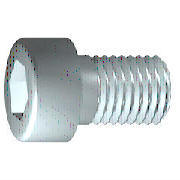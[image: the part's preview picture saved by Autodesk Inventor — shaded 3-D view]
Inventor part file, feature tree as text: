
AUTODESK INVENTOR PART (.ipt)
format: ipt  version: 2015 (Build 190159000, 159)  size: 190,464 bytes
history: native  units: mm (DEFAULTED — no unit token found)
features: sketch x2, other x1, extrude x1, plane x1, fillet x1
ambient origin geometry x7: Origin, YZ Plane, XY Plane, X Axis, Y Axis, Z Axis, Center Point
bodies: Body1 (feature_tree)
feature tree (6):
  other  "Bryła"
  extrude  "Szczelina"  Depth=27.5mm
  plane  "Work Plane1"
  fillet  "Fillet2"  Radius=0.61355mm
  sketch  "Szkic1"
  sketch  "Szkic2"
